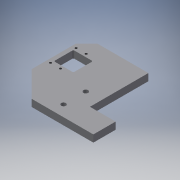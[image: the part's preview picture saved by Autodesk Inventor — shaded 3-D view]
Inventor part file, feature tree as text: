
AUTODESK INVENTOR PART (.ipt)
format: ipt  version: 2018 (Build 220112000, 112)  size: 171,520 bytes
history: native  units: mm
features: sketch x5, hole x3, extrude x2, other x1, chamfer x1
ambient origin geometry x8: Origin, YZ Plane, XZ Plane, XY Plane, X Axis, Y Axis, Z Axis, Center Point
bodies: Body1 (feature_tree)
feature tree (12):
  other  "Sólido1"
  extrude  "Extrusão1"  Depth=40.0mm
  chamfer  "Chanfro1"  Distance=12.7mm
  hole  "Furo1"  [1 undecoded]
  extrude  "Extrusão2"  Depth=35.0mm
  hole  "Furo2"  [1 undecoded]
  hole  "Furo3"  [1 undecoded]
  sketch  "Esboço1"  dims[d0=111.0mm d5=40.0mm]
  sketch  "Esboço2"  dims[d6=105.0mm]
  sketch  "Esboço3"  dims[d7=135.0deg]
  sketch  "Esboço4"  dims[d8=98.71536mm d9=12.7mm d10=0.0mm]
  sketch  "Esboço5"  dims[d11=157.066236mm d12=20.0mm d13=2.0mm d14=45.0deg d15=4.134mm d16=10.0mm d17=4.0mm d18=2.0mm d19=90.0deg d20=14.2mm d21=20.594885mm d22=35.0mm d23=35.0mm d24=2.0mm d25=10.0mm d26=0.0mm d27=8.0mm d28=8.0mm d29=8.5mm d30=10.0mm d31=4.0mm d32=2.0mm d33=90.0deg d34=14.2mm d35=20.594885mm d36=27.5mm d37=60.0mm d38=20.0mm d39=27.5mm d40=26.5mm d41=13.25mm d42=13.25mm d43=53.0mm d44=5.0mm d45=5.0mm d46=5.5mm d47=10.0mm d48=4.0mm d49=2.0mm d50=90.0deg d51=14.2mm d52=20.594885mm]
note: 3 required parameter values undecoded (feature->parameter linkage not recoverable at this tier; creation-order binding heuristic only, values carry confidence <= 0.55)
